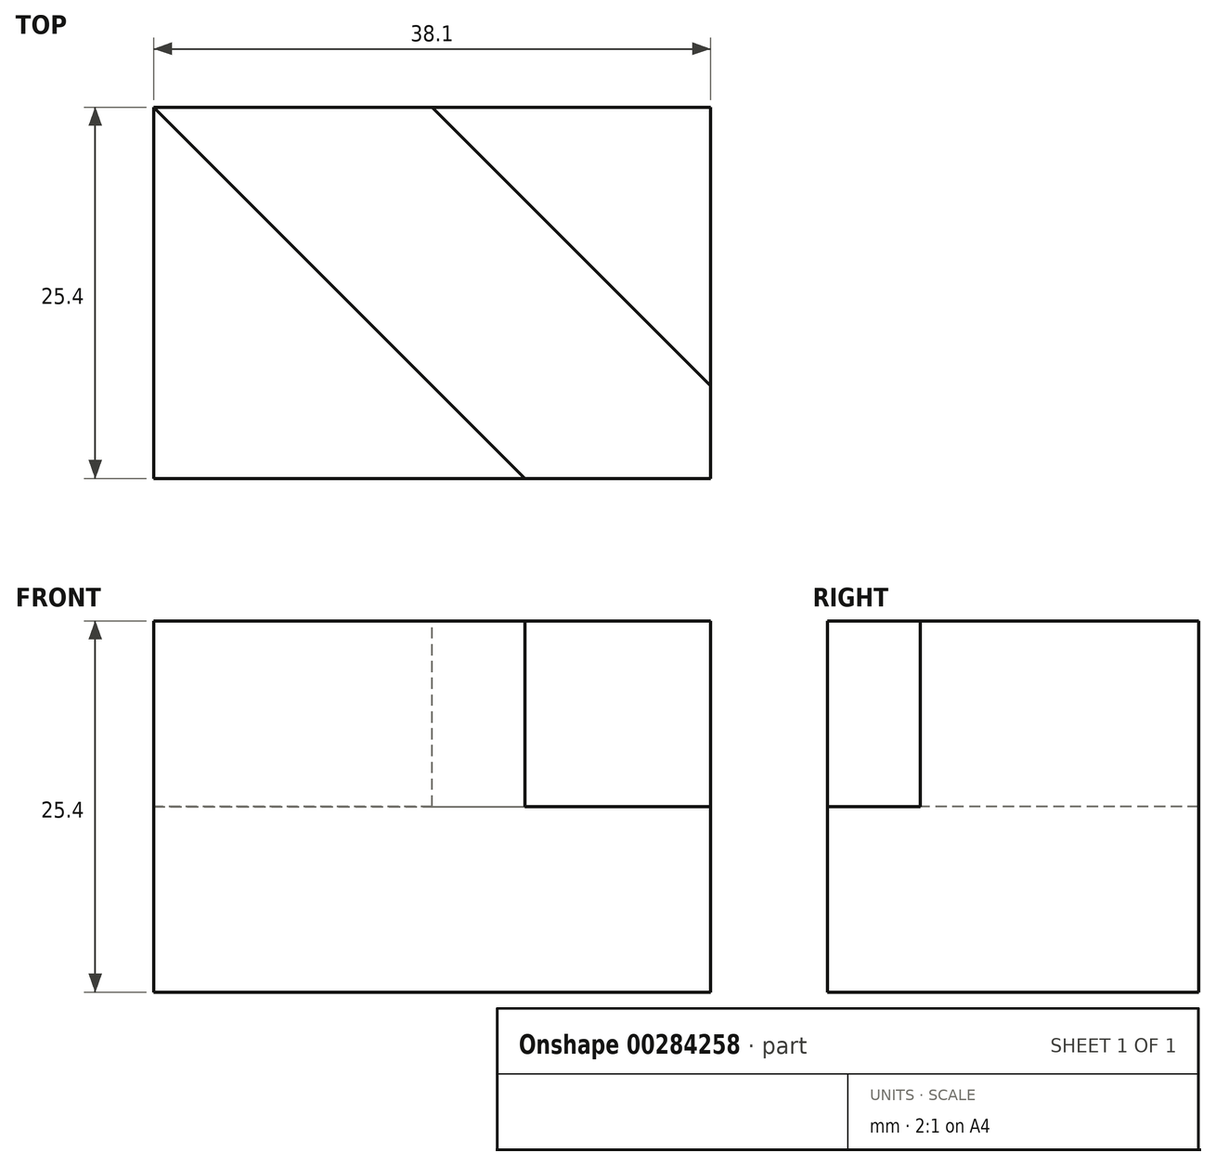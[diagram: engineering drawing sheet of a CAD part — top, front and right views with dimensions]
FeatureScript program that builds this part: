
annotation { "Feature Type Name" : "Feature", "Feature Type Description" : "" }
export const myFeature = defineFeature(function(context is Context, id is Id, definition is map)
    precondition{}
    {
        {
            var Q0;
            Q0=qCreatedBy(makeId("Front.planeOp"),FACE);
            var sketch = newSketch(context, id + "F0", { "sketchPlane" : qUnion([Q0])});
            skLineSegment(sketch, "E0", {"start": v(0, 0) * mm, "end": v(38.1, 0) * mm});
            skLineSegment(sketch, "E1", {"start": v(38.1, 0) * mm, "end": v(38.1, 25.4) * mm});
            skLineSegment(sketch, "E2", {"start": v(38.1, 25.4) * mm, "end": v(0, 25.4) * mm});
            skLineSegment(sketch, "E3", {"start": v(0, 25.4) * mm, "end": v(0, 0) * mm});
            skSolve(sketch);
        }
        {
            var Q0;
            Q0=makeQuery(id+"F0.imprint","IMPRINT",FACE,{"disambiguationData":[TD([[makeQuery(id+"F0.imprint","IMPRINT",EDGE,{"derivedFrom":sQuery(id+"F0.wireOp",EDGE,"E0")}),1.0]])]});
            extrude(context, id + "F1", {"entities" : qUnion([Q0]), "depth" : 25.4 * mm});
        }
        {
            var Q0;
            Q0=makeQuery(id+"F1.opExtrude","SWEPT_FACE",FACE,{"disambiguationData":[OSD([sQuery(id+"F0.wireOp",EDGE,"E2")])]});
            var sketch = newSketch(context, id + "F2", { "sketchPlane" : qUnion([Q0])});
            skLineSegment(sketch, "E4", {"start": v(0, 0) * mm, "end": v(25.4, -25.4) * mm});
            skLineSegment(sketch, "E5", {"start": v(19.05, 0) * mm, "end": v(38.1, -19.05) * mm});
            skSolve(sketch);
        }
        {
            var Q0;
            {var subQ5=sQuery(id+"F2.wireOp",EDGE,"E4");Q0=makeQuery(id+"F2.imprint","IMPRINT",FACE,{"disambiguationData":[TD([[makeQuery(id+"F2.imprint","IMPRINT",EDGE,{"derivedFrom":subQ5}),1.0]])]});}
            extrude(context, id + "F3", {"entities" : qUnion([Q0]), "operationType" : NewBodyOperationType.REMOVE, "oppositeDirection" : true, "depth" : 12.7 * mm});
        }
    });
